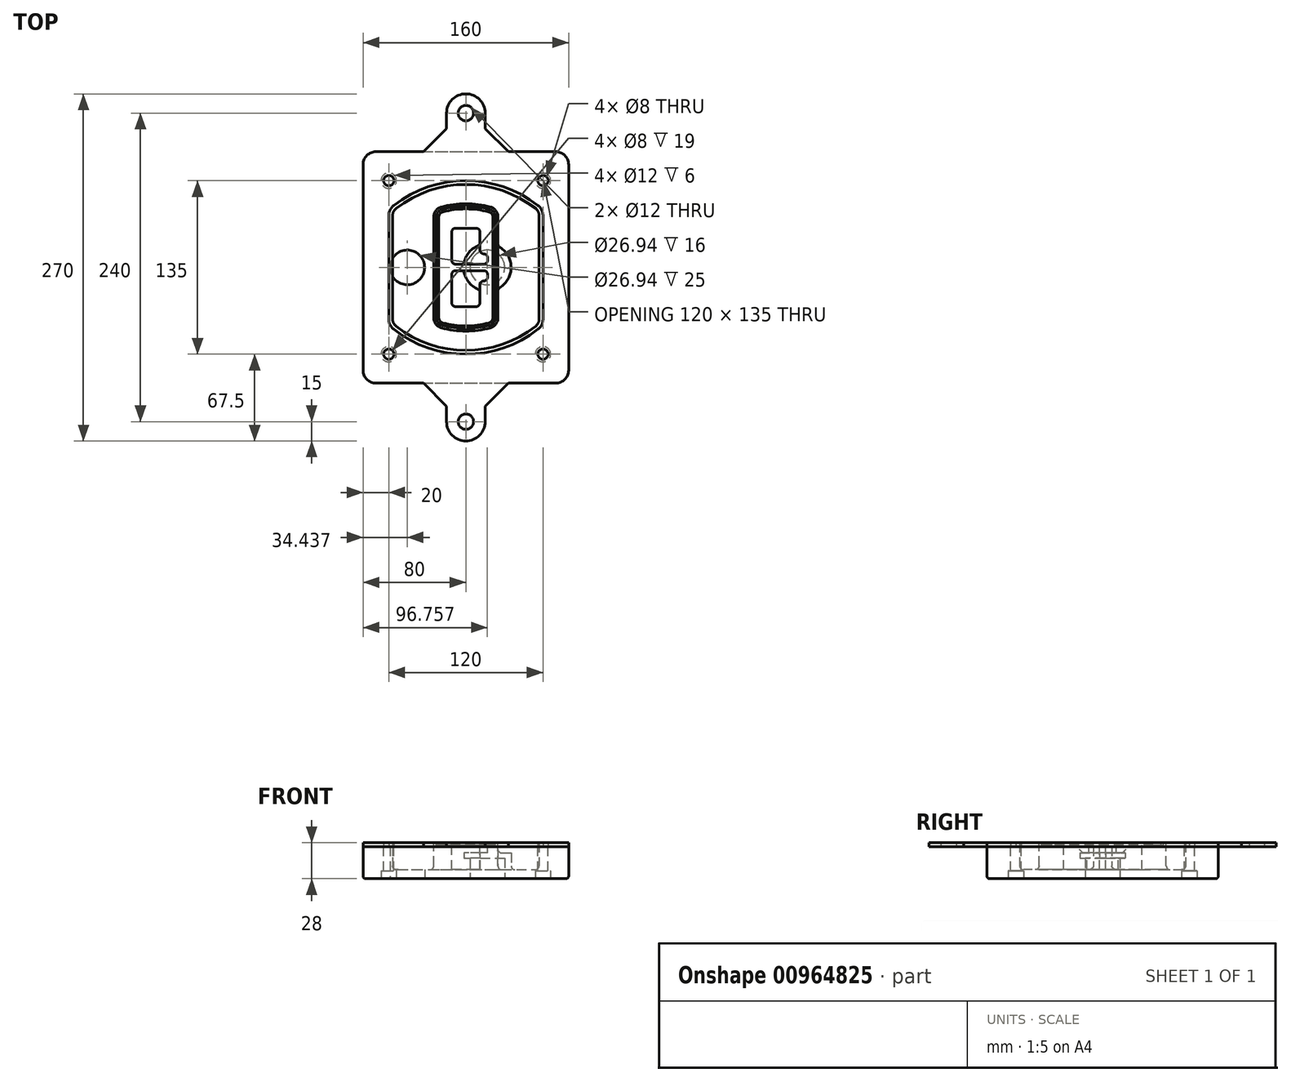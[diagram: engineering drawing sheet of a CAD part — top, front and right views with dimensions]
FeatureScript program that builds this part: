
annotation { "Feature Type Name" : "Feature", "Feature Type Description" : "" }
export const myFeature = defineFeature(function(context is Context, id is Id, definition is map)
    precondition{}
    {
        {
            var Q0;
            Q0=qCreatedBy(makeId("Top.planeOp"),FACE);
            var sketch = newSketch(context, id + "F0", { "sketchPlane" : qUnion([Q0])});
            skPoint(sketch, "E0.rect.middle", {"position": v(0, 0) * mm});
            skLineSegment(sketch, "E1.bottom", {"start": v(-70, -90) * mm, "end": v(70, -90) * mm});
            skLineSegment(sketch, "E1.top", {"start": v(-70, 90) * mm, "end": v(70, 90) * mm});
            skLineSegment(sketch, "E1.left", {"start": v(-80, -80) * mm, "end": v(-80, 80) * mm});
            skLineSegment(sketch, "E1.right", {"start": v(80, -80) * mm, "end": v(80, 80) * mm});
            skLineSegment(sketch, "E2", {"start": v(-80, 90) * mm, "end": v(80, -90) * mm, "construction": true});
            skLineSegment(sketch, "E3", {"start": v(80, 90) * mm, "end": v(-80, -90) * mm, "construction": true});
            skCircle(sketch, "E4", {"center": v(-60, 67.5) * mm, "radius": 4 * mm});
            skCircle(sketch, "E5", {"center": v(60, 67.5) * mm, "radius": 4 * mm});
            skCircle(sketch, "E6", {"center": v(60, -67.5) * mm, "radius": 4 * mm});
            skCircle(sketch, "E7", {"center": v(-60, -67.5) * mm, "radius": 4 * mm});
            skLineSegment(sketch, "E8", {"start": v(-60, 67.5) * mm, "end": v(60, 67.5) * mm, "construction": true});
            skLineSegment(sketch, "E9", {"start": v(60, 67.5) * mm, "end": v(60, -67.5) * mm, "construction": true});
            skLineSegment(sketch, "E10", {"start": v(60, -67.5) * mm, "end": v(-60, -67.5) * mm, "construction": true});
            skLineSegment(sketch, "E11", {"start": v(-60, -67.5) * mm, "end": v(-60, 67.5) * mm, "construction": true});
            skLineSegment(sketch, "E12", {"start": v(-60, 40.3) * mm, "end": v(-60, -40.3) * mm});
            skLineSegment(sketch, "E13", {"start": v(60, 40.3) * mm, "end": v(60, -40.3) * mm});
            skArc(sketch, "E14", {"start": v(56.15, 48.18) * mm, "mid": v(0, 67.5) * mm, "end": v(-56.15, 48.18) * mm});
            skArc(sketch, "E15", {"start": v(-56.15, -48.18) * mm, "mid": v(0, -67.5) * mm, "end": v(56.15, -48.18) * mm});
            skLineSegment(sketch, "E16", {"start": v(-60, 0) * mm, "end": v(60, 0) * mm, "construction": true});
            skPoint(sketch, "E17.visualSharp", {"position": v(-60, -45) * mm});
            skArc(sketch, "E17.filletArc", {"start": v(-60, -40.3) * mm, "mid": v(-58.99, -44.68) * mm, "end": v(-56.15, -48.18) * mm});
            skPoint(sketch, "E18.visualSharp", {"position": v(-60, 45) * mm});
            skArc(sketch, "E18.filletArc", {"start": v(-56.15, 48.18) * mm, "mid": v(-58.99, 44.68) * mm, "end": v(-60, 40.3) * mm});
            skPoint(sketch, "E19.visualSharp", {"position": v(60, 45) * mm});
            skArc(sketch, "E19.filletArc", {"start": v(60, 40.3) * mm, "mid": v(58.99, 44.68) * mm, "end": v(56.15, 48.18) * mm});
            skPoint(sketch, "E20.visualSharp", {"position": v(60, -45) * mm});
            skArc(sketch, "E20.filletArc", {"start": v(56.15, -48.18) * mm, "mid": v(58.99, -44.68) * mm, "end": v(60, -40.3) * mm});
            skPoint(sketch, "E21.visualSharp", {"position": v(-80, 90) * mm});
            skArc(sketch, "E21.filletArc", {"start": v(-70, 90) * mm, "mid": v(-77.07, 87.07) * mm, "end": v(-80, 80) * mm});
            skPoint(sketch, "E22.visualSharp", {"position": v(80, 90) * mm});
            skArc(sketch, "E22.filletArc", {"start": v(80, 80) * mm, "mid": v(77.07, 87.07) * mm, "end": v(70, 90) * mm});
            skPoint(sketch, "E23.visualSharp", {"position": v(80, -90) * mm});
            skArc(sketch, "E23.filletArc", {"start": v(70, -90) * mm, "mid": v(77.07, -87.07) * mm, "end": v(80, -80) * mm});
            skPoint(sketch, "E24.visualSharp", {"position": v(-80, -90) * mm});
            skArc(sketch, "E24.filletArc", {"start": v(-80, -80) * mm, "mid": v(-77.07, -87.07) * mm, "end": v(-70, -90) * mm});
            skArc(sketch, "E25.0", {"start": v(57, 40.3) * mm, "mid": v(56.3, 43.36) * mm, "end": v(54.3, 45.81) * mm});
            skLineSegment(sketch, "E25.1", {"start": v(57, 40.3) * mm, "end": v(57, -40.3) * mm});
            skArc(sketch, "E25.2", {"start": v(54.3, -45.81) * mm, "mid": v(56.3, -43.36) * mm, "end": v(57, -40.3) * mm});
            skArc(sketch, "E25.3", {"start": v(-54.3, -45.81) * mm, "mid": v(0, -64.5) * mm, "end": v(54.3, -45.81) * mm});
            skArc(sketch, "E25.4", {"start": v(-57, -40.3) * mm, "mid": v(-56.3, -43.36) * mm, "end": v(-54.3, -45.81) * mm});
            skArc(sketch, "E25.5", {"start": v(54.3, 45.81) * mm, "mid": v(0, 64.5) * mm, "end": v(-54.3, 45.81) * mm});
            skLineSegment(sketch, "E25.6", {"start": v(-57, 40.3) * mm, "end": v(-57, -40.3) * mm});
            skArc(sketch, "E25.7", {"start": v(-54.3, 45.81) * mm, "mid": v(-56.3, 43.36) * mm, "end": v(-57, 40.3) * mm});
            skArc(sketch, "E26.0", {"start": v(-58.62, 51.33) * mm, "mid": v(-62.58, 46.43) * mm, "end": v(-64, 40.3) * mm});
            skArc(sketch, "E26.1", {"start": v(58.62, 51.33) * mm, "mid": v(0, 71.5) * mm, "end": v(-58.62, 51.33) * mm});
            skArc(sketch, "E26.2", {"start": v(64, 40.3) * mm, "mid": v(62.58, 46.43) * mm, "end": v(58.62, 51.33) * mm});
            skLineSegment(sketch, "E26.3", {"start": v(64, 40.3) * mm, "end": v(64, -40.3) * mm});
            skArc(sketch, "E26.4", {"start": v(58.62, -51.33) * mm, "mid": v(62.58, -46.43) * mm, "end": v(64, -40.3) * mm});
            skLineSegment(sketch, "E26.5", {"start": v(-64, 40.3) * mm, "end": v(-64, -40.3) * mm});
            skArc(sketch, "E26.6", {"start": v(-58.62, -51.33) * mm, "mid": v(0, -71.5) * mm, "end": v(58.62, -51.33) * mm});
            skArc(sketch, "E26.7", {"start": v(-64, -40.3) * mm, "mid": v(-62.58, -46.43) * mm, "end": v(-58.62, -51.33) * mm});
            skSolve(sketch);
        }
        {
            var Q0;
            Q0=makeQuery(id+"F0.imprint","IMPRINT",FACE,{"disambiguationData":[TD([[makeQuery(id+"F0.imprint","IMPRINT",EDGE,{"derivedFrom":sQuery(id+"F0.wireOp",EDGE,"E1.bottom")}),1.0]])]});
            var Q1;
            Q1=makeQuery(id+"F0.imprint","IMPRINT",FACE,{"disambiguationData":[TD([[makeQuery(id+"F0.imprint","IMPRINT",EDGE,{"derivedFrom":sQuery(id+"F0.wireOp",EDGE,"E12")}),1.0]])]});
            var Q2;
            Q2=makeQuery(id+"F0.imprint","IMPRINT",FACE,{"disambiguationData":[TD([[makeQuery(id+"F0.imprint","IMPRINT",EDGE,{"derivedFrom":sQuery(id+"F0.wireOp",EDGE,"E25.0")}),1.0]])]});
            var Q3;
            Q3=makeQuery(id+"F0.imprint","IMPRINT",FACE,{"disambiguationData":[TD([[makeQuery(id+"F0.imprint","IMPRINT",EDGE,{"derivedFrom":sQuery(id+"F0.wireOp",EDGE,"E12")}),-1.0]])]});
            extrude(context, id + "F1", {"entities" : qUnion([Q0, Q1, Q2, Q3]), "oppositeDirection" : true, "depth" : 25 * mm});
        }
        {
            var Q0;
            Q0=makeQuery(id+"F0.imprint","IMPRINT",FACE,{"disambiguationData":[TD([[makeQuery(id+"F0.imprint","IMPRINT",EDGE,{"derivedFrom":sQuery(id+"F0.wireOp",EDGE,"E12")}),1.0]])]});
            extrude(context, id + "F2", {"entities" : qUnion([Q0]), "operationType" : NewBodyOperationType.ADD, "depth" : 3 * mm});
        }
        {
            var Q0;
            Q0=makeQuery(id+"F0.imprint","IMPRINT",FACE,{"disambiguationData":[TD([[makeQuery(id+"F0.imprint","IMPRINT",EDGE,{"derivedFrom":sQuery(id+"F0.wireOp",EDGE,"E25.0")}),1.0]])]});
            extrude(context, id + "F3", {"entities" : qUnion([Q0]), "operationType" : NewBodyOperationType.REMOVE, "oppositeDirection" : true, "depth" : 18 * mm});
        }
        {
            var Q0;
            Q0=makeQuery(id+"F2.opExtrude","CAP_FACE",FACE,{"disambiguationData":[OSD([sQuery(id+"F0.wireOp",EDGE,"E12"),sQuery(id+"F0.wireOp",EDGE,"E13"),sQuery(id+"F0.wireOp",EDGE,"E14"),sQuery(id+"F0.wireOp",EDGE,"E15"),sQuery(id+"F0.wireOp",EDGE,"E17.filletArc"),sQuery(id+"F0.wireOp",EDGE,"E18.filletArc"),sQuery(id+"F0.wireOp",EDGE,"E19.filletArc"),sQuery(id+"F0.wireOp",EDGE,"E20.filletArc"),sQuery(id+"F0.wireOp",EDGE,"E25.0"),sQuery(id+"F0.wireOp",EDGE,"E25.1"),sQuery(id+"F0.wireOp",EDGE,"E25.2"),sQuery(id+"F0.wireOp",EDGE,"E25.3"),sQuery(id+"F0.wireOp",EDGE,"E25.4"),sQuery(id+"F0.wireOp",EDGE,"E25.5"),sQuery(id+"F0.wireOp",EDGE,"E25.6"),sQuery(id+"F0.wireOp",EDGE,"E25.7")])],"isStart":false});
            var sketch = newSketch(context, id + "F4", { "sketchPlane" : qUnion([Q0])});
            skArc(sketch, "E27.0", {"start": v(-19.08, -46.97) * mm, "mid": v(0, -49.5) * mm, "end": v(19.08, -46.97) * mm});
            skArc(sketch, "E28.0", {"start": v(19.08, 46.97) * mm, "mid": v(0, 49.5) * mm, "end": v(-19.08, 46.97) * mm});
            skLineSegment(sketch, "E29", {"start": v(-25, 39.25) * mm, "end": v(-25, -39.25) * mm});
            skLineSegment(sketch, "E30", {"start": v(25, 39.25) * mm, "end": v(25, -39.25) * mm});
            skLineSegment(sketch, "E31", {"start": v(-25, 45.1) * mm, "end": v(25, 45.1) * mm, "construction": true});
            skLineSegment(sketch, "E32", {"start": v(-25, -45.1) * mm, "end": v(25, -45.1) * mm, "construction": true});
            skPoint(sketch, "E33.visualSharp", {"position": v(-25, 45.1) * mm});
            skArc(sketch, "E33.filletArc", {"start": v(-19.08, 46.97) * mm, "mid": v(-23.35, 44.11) * mm, "end": v(-25, 39.25) * mm});
            skPoint(sketch, "E34.visualSharp", {"position": v(25, 45.1) * mm});
            skArc(sketch, "E34.filletArc", {"start": v(25, 39.25) * mm, "mid": v(23.35, 44.11) * mm, "end": v(19.08, 46.97) * mm});
            skPoint(sketch, "E35.visualSharp", {"position": v(25, -45.1) * mm});
            skArc(sketch, "E35.filletArc", {"start": v(19.08, -46.97) * mm, "mid": v(23.35, -44.11) * mm, "end": v(25, -39.25) * mm});
            skPoint(sketch, "E36.visualSharp", {"position": v(-25, -45.1) * mm});
            skArc(sketch, "E36.filletArc", {"start": v(-25, -39.25) * mm, "mid": v(-23.35, -44.11) * mm, "end": v(-19.08, -46.97) * mm});
            skArc(sketch, "E37.0", {"start": v(54.3, 45.81) * mm, "mid": v(0, 64.5) * mm, "end": v(-54.3, 45.81) * mm});
            skArc(sketch, "E37.1", {"start": v(-54.3, 45.81) * mm, "mid": v(-56.3, 43.36) * mm, "end": v(-57, 40.3) * mm});
            skLineSegment(sketch, "E37.2", {"start": v(-57, 40.3) * mm, "end": v(-57, -40.3) * mm});
            skArc(sketch, "E37.3", {"start": v(-57, -40.3) * mm, "mid": v(-56.3, -43.36) * mm, "end": v(-54.3, -45.81) * mm});
            skArc(sketch, "E37.4", {"start": v(-54.3, -45.81) * mm, "mid": v(0, -64.5) * mm, "end": v(54.3, -45.81) * mm});
            skArc(sketch, "E37.5", {"start": v(54.3, -45.81) * mm, "mid": v(56.3, -43.36) * mm, "end": v(57, -40.3) * mm});
            skLineSegment(sketch, "E37.6", {"start": v(57, 40.3) * mm, "end": v(57, -40.3) * mm});
            skArc(sketch, "E37.7", {"start": v(57, 40.3) * mm, "mid": v(56.3, 43.36) * mm, "end": v(54.3, 45.81) * mm});
            skLineSegment(sketch, "E38.0", {"start": v(23, 39.25) * mm, "end": v(23, -39.25) * mm});
            skArc(sketch, "E38.1", {"start": v(18.56, -45.04) * mm, "mid": v(21.76, -42.9) * mm, "end": v(23, -39.25) * mm});
            skArc(sketch, "E38.2", {"start": v(-18.56, -45.04) * mm, "mid": v(0, -47.5) * mm, "end": v(18.56, -45.04) * mm});
            skArc(sketch, "E38.3", {"start": v(-23, -39.25) * mm, "mid": v(-21.76, -42.9) * mm, "end": v(-18.56, -45.04) * mm});
            skLineSegment(sketch, "E38.4", {"start": v(-23, 39.25) * mm, "end": v(-23, -39.25) * mm});
            skArc(sketch, "E38.5", {"start": v(23, 39.25) * mm, "mid": v(21.76, 42.9) * mm, "end": v(18.56, 45.04) * mm});
            skArc(sketch, "E38.6", {"start": v(-18.56, 45.04) * mm, "mid": v(-21.76, 42.9) * mm, "end": v(-23, 39.25) * mm});
            skArc(sketch, "E38.7", {"start": v(18.56, 45.04) * mm, "mid": v(0, 47.5) * mm, "end": v(-18.56, 45.04) * mm});
            skArc(sketch, "E39.0", {"start": v(21, 39.25) * mm, "mid": v(20.18, 41.68) * mm, "end": v(18.04, 43.1) * mm});
            skLineSegment(sketch, "E39.1", {"start": v(21, 39.25) * mm, "end": v(21, -39.25) * mm});
            skArc(sketch, "E39.2", {"start": v(18.04, -43.1) * mm, "mid": v(20.18, -41.68) * mm, "end": v(21, -39.25) * mm});
            skArc(sketch, "E39.3", {"start": v(-18.04, -43.1) * mm, "mid": v(0, -45.5) * mm, "end": v(18.04, -43.1) * mm});
            skArc(sketch, "E39.4", {"start": v(-21, -39.25) * mm, "mid": v(-20.18, -41.68) * mm, "end": v(-18.04, -43.1) * mm});
            skArc(sketch, "E39.5", {"start": v(18.04, 43.1) * mm, "mid": v(0, 45.5) * mm, "end": v(-18.04, 43.1) * mm});
            skLineSegment(sketch, "E39.6", {"start": v(-21, 39.25) * mm, "end": v(-21, -39.25) * mm});
            skArc(sketch, "E39.7", {"start": v(-18.04, 43.1) * mm, "mid": v(-20.18, 41.68) * mm, "end": v(-21, 39.25) * mm});
            skLineSegment(sketch, "E40", {"start": v(-25, 0) * mm, "end": v(25, 0) * mm, "construction": true});
            skLineSegment(sketch, "E41", {"start": v(-11, 5.5) * mm, "end": v(-11, 27.5) * mm});
            skLineSegment(sketch, "E42", {"start": v(-8, 30.5) * mm, "end": v(8, 30.5) * mm});
            skLineSegment(sketch, "E43", {"start": v(11, 27.5) * mm, "end": v(11, 13.5) * mm});
            skLineSegment(sketch, "E44", {"start": v(14, 10.5) * mm, "end": v(14, 10.5) * mm});
            skLineSegment(sketch, "E45", {"start": v(17, 7.5) * mm, "end": v(17, 5.5) * mm});
            skLineSegment(sketch, "E46", {"start": v(14, 2.5) * mm, "end": v(-8, 2.5) * mm});
            skPoint(sketch, "E47.visualSharp", {"position": v(-11, 30.5) * mm});
            skArc(sketch, "E47.filletArc", {"start": v(-8, 30.5) * mm, "mid": v(-10.12, 29.62) * mm, "end": v(-11, 27.5) * mm});
            skPoint(sketch, "E48.visualSharp", {"position": v(11, 30.5) * mm});
            skArc(sketch, "E48.filletArc", {"start": v(11, 27.5) * mm, "mid": v(10.12, 29.62) * mm, "end": v(8, 30.5) * mm});
            skPoint(sketch, "E49.visualSharp", {"position": v(11, 10.5) * mm});
            skArc(sketch, "E49.filletArc", {"start": v(11, 13.5) * mm, "mid": v(11.88, 11.38) * mm, "end": v(14, 10.5) * mm});
            skPoint(sketch, "E50.visualSharp", {"position": v(17, 10.5) * mm});
            skArc(sketch, "E50.filletArc", {"start": v(17, 7.5) * mm, "mid": v(16.12, 9.62) * mm, "end": v(14, 10.5) * mm});
            skPoint(sketch, "E51.visualSharp", {"position": v(17, 2.5) * mm});
            skArc(sketch, "E51.filletArc", {"start": v(14, 2.5) * mm, "mid": v(16.12, 3.38) * mm, "end": v(17, 5.5) * mm});
            skPoint(sketch, "E52.visualSharp", {"position": v(-11, 2.5) * mm});
            skArc(sketch, "E52.filletArc", {"start": v(-11, 5.5) * mm, "mid": v(-10.12, 3.38) * mm, "end": v(-8, 2.5) * mm});
            skLineSegment(sketch, "E53.0.MirrorCS", {"start": v(14, -2.5) * mm, "end": v(-8, -2.5) * mm});
            skArc(sketch, "E54.0.MirrorCS", {"start": v(-11, -5.5) * mm, "mid": v(-10.12, -3.38) * mm, "end": v(-8, -2.5) * mm});
            skLineSegment(sketch, "E55.0.MirrorCS", {"start": v(-11, -5.5) * mm, "end": v(-11, -27.5) * mm});
            skArc(sketch, "E56.0.MirrorCS", {"start": v(-8, -30.5) * mm, "mid": v(-10.12, -29.62) * mm, "end": v(-11, -27.5) * mm});
            skLineSegment(sketch, "E57.0.MirrorCS", {"start": v(-8, -30.5) * mm, "end": v(8, -30.5) * mm});
            skArc(sketch, "E58.0.MirrorCS", {"start": v(11, -27.5) * mm, "mid": v(10.12, -29.62) * mm, "end": v(8, -30.5) * mm});
            skLineSegment(sketch, "E59.0.MirrorCS", {"start": v(11, -27.5) * mm, "end": v(11, -13.5) * mm});
            skArc(sketch, "E60.0.MirrorCS", {"start": v(11, -13.5) * mm, "mid": v(11.88, -11.38) * mm, "end": v(14, -10.5) * mm});
            skArc(sketch, "E61.0.MirrorCS", {"start": v(17, -7.5) * mm, "mid": v(16.12, -9.62) * mm, "end": v(14, -10.5) * mm});
            skLineSegment(sketch, "E62.0.MirrorCS", {"start": v(17, -7.5) * mm, "end": v(17, -5.5) * mm});
            skArc(sketch, "E63.0.MirrorCS", {"start": v(14, -2.5) * mm, "mid": v(16.12, -3.38) * mm, "end": v(17, -5.5) * mm});
            skSolve(sketch);
        }
        {
            var Q0;
            Q0=makeQuery(id+"F4.imprint","IMPRINT",FACE,{"disambiguationData":[TD([[makeQuery(id+"F4.imprint","IMPRINT",EDGE,{"derivedFrom":sQuery(id+"F4.wireOp",EDGE,"E27.0")}),1.0]])]});
            var Q1;
            Q1=makeQuery(id+"F4.imprint","IMPRINT",FACE,{"disambiguationData":[TD([[makeQuery(id+"F4.imprint","IMPRINT",EDGE,{"derivedFrom":sQuery(id+"F4.wireOp",EDGE,"E38.0")}),-1.0]])]});
            var Q2;
            Q2=makeQuery(id+"F4.imprint","IMPRINT",FACE,{"disambiguationData":[TD([[makeQuery(id+"F4.imprint","IMPRINT",EDGE,{"derivedFrom":sQuery(id+"F4.wireOp",EDGE,"E39.0")}),1.0]])]});
            extrude(context, id + "F5", {"entities" : qUnion([Q0, Q1, Q2]), "operationType" : NewBodyOperationType.ADD, "endBound" : BoundingType.UP_TO_NEXT, "oppositeDirection" : true, "depth" : 25 * mm});
        }
        {
            var Q0;
            Q0=makeQuery(id+"F4.imprint","IMPRINT",FACE,{"disambiguationData":[TD([[makeQuery(id+"F4.imprint","IMPRINT",EDGE,{"derivedFrom":sQuery(id+"F4.wireOp",EDGE,"E38.0")}),-1.0]])]});
            extrude(context, id + "F6", {"entities" : qUnion([Q0]), "operationType" : NewBodyOperationType.REMOVE, "oppositeDirection" : true, "depth" : 2 * mm});
        }
        {
            var Q0;
            Q0=makeQuery(id+"F1.opExtrude","CAP_FACE",FACE,{"disambiguationData":[OSD([sQuery(id+"F0.wireOp",EDGE,"E1.bottom"),sQuery(id+"F0.wireOp",EDGE,"E1.top"),sQuery(id+"F0.wireOp",EDGE,"E1.left"),sQuery(id+"F0.wireOp",EDGE,"E1.right"),sQuery(id+"F0.wireOp",EDGE,"E4"),sQuery(id+"F0.wireOp",EDGE,"E5"),sQuery(id+"F0.wireOp",EDGE,"E6"),sQuery(id+"F0.wireOp",EDGE,"E7"),sQuery(id+"F0.wireOp",EDGE,"E21.filletArc"),sQuery(id+"F0.wireOp",EDGE,"E22.filletArc"),sQuery(id+"F0.wireOp",EDGE,"E23.filletArc"),sQuery(id+"F0.wireOp",EDGE,"E24.filletArc")])],"isStart":false});
            var sketch = newSketch(context, id + "F7", { "sketchPlane" : qUnion([Q0])});
            skCircle(sketch, "E64", {"center": v(16.76, 0) * mm, "radius": 13.47 * mm});
            skCircle(sketch, "E65", {"center": v(-45.56, 0) * mm, "radius": 13.47 * mm});
            skLineSegment(sketch, "E66", {"start": v(80, 0) * mm, "end": v(-80, 0) * mm});
            skCircle(sketch, "E67", {"center": v(16.76, 0) * mm, "radius": 18.47 * mm});
            skCircle(sketch, "E68", {"center": v(60, -67.5) * mm, "radius": 6 * mm});
            skCircle(sketch, "E69", {"center": v(-60, -67.5) * mm, "radius": 6 * mm});
            skCircle(sketch, "E70", {"center": v(-60, 67.5) * mm, "radius": 6 * mm});
            skCircle(sketch, "E71", {"center": v(60, 67.5) * mm, "radius": 6 * mm});
            skSolve(sketch);
        }
        {
            var Q0;
            {var subQ1=sQuery(id+"F7.wireOp",EDGE,"E66");var subQ4=sQuery(id+"F7.wireOp",EDGE,"E64");var subQ6=makeQuery(id+"F7.imprint","INTERSECT",VERTEX,{"disambiguationData":[OD(0.0)],"derivedFrom":[subQ4,subQ1]});Q0=makeQuery(id+"F7.imprint","IMPRINT",FACE,{"disambiguationData":[TD([[makeQuery(id+"F7.imprint","IMPRINT",EDGE,{"disambiguationData":[TD([[subQ6,-1.0]])],"derivedFrom":subQ4}),-1.0]])]});}
            var Q1;
            {var subQ0=sQuery(id+"F7.wireOp",EDGE,"E66");var subQ1=sQuery(id+"F7.wireOp",EDGE,"E64");var subQ3=makeQuery(id+"F7.imprint","INTERSECT",VERTEX,{"disambiguationData":[OD(0.0)],"derivedFrom":[subQ1,subQ0]});Q1=makeQuery(id+"F7.imprint","IMPRINT",FACE,{"disambiguationData":[TD([[makeQuery(id+"F7.imprint","IMPRINT",EDGE,{"disambiguationData":[TD([[subQ3,-1.0]])],"derivedFrom":subQ1}),1.0]])]});}
            var Q2;
            {var subQ0=sQuery(id+"F7.wireOp",EDGE,"E66");var subQ1=sQuery(id+"F7.wireOp",EDGE,"E64");var subQ3=makeQuery(id+"F7.imprint","INTERSECT",VERTEX,{"disambiguationData":[OD(0.0)],"derivedFrom":[subQ1,subQ0]});Q2=makeQuery(id+"F7.imprint","IMPRINT",FACE,{"disambiguationData":[TD([[makeQuery(id+"F7.imprint","IMPRINT",EDGE,{"disambiguationData":[TD([[subQ3,1.0]])],"derivedFrom":subQ1}),1.0]])]});}
            var Q3;
            {var subQ1=sQuery(id+"F7.wireOp",EDGE,"E66");var subQ4=sQuery(id+"F7.wireOp",EDGE,"E64");var subQ6=makeQuery(id+"F7.imprint","INTERSECT",VERTEX,{"disambiguationData":[OD(0.0)],"derivedFrom":[subQ4,subQ1]});Q3=makeQuery(id+"F7.imprint","IMPRINT",FACE,{"disambiguationData":[TD([[makeQuery(id+"F7.imprint","IMPRINT",EDGE,{"disambiguationData":[TD([[subQ6,1.0]])],"derivedFrom":subQ4}),-1.0]])]});}
            extrude(context, id + "F8", {"entities" : qUnion([Q0, Q1, Q2, Q3]), "operationType" : NewBodyOperationType.ADD, "oppositeDirection" : true, "depth" : 20 * mm});
        }
        {
            var Q0;
            {var subQ0=sQuery(id+"F7.wireOp",EDGE,"E66");var subQ1=sQuery(id+"F7.wireOp",EDGE,"E64");var subQ3=makeQuery(id+"F7.imprint","INTERSECT",VERTEX,{"disambiguationData":[OD(0.0)],"derivedFrom":[subQ1,subQ0]});Q0=makeQuery(id+"F7.imprint","IMPRINT",FACE,{"disambiguationData":[TD([[makeQuery(id+"F7.imprint","IMPRINT",EDGE,{"disambiguationData":[TD([[subQ3,-1.0]])],"derivedFrom":subQ1}),1.0]])]});}
            var Q1;
            {var subQ0=sQuery(id+"F7.wireOp",EDGE,"E66");var subQ1=sQuery(id+"F7.wireOp",EDGE,"E64");var subQ3=makeQuery(id+"F7.imprint","INTERSECT",VERTEX,{"disambiguationData":[OD(0.0)],"derivedFrom":[subQ1,subQ0]});Q1=makeQuery(id+"F7.imprint","IMPRINT",FACE,{"disambiguationData":[TD([[makeQuery(id+"F7.imprint","IMPRINT",EDGE,{"disambiguationData":[TD([[subQ3,1.0]])],"derivedFrom":subQ1}),1.0]])]});}
            extrude(context, id + "F9", {"entities" : qUnion([Q0, Q1]), "operationType" : NewBodyOperationType.REMOVE, "oppositeDirection" : true, "depth" : 16 * mm});
        }
        {
            var Q0;
            {var subQ0=sQuery(id+"F7.wireOp",EDGE,"E66");var subQ1=sQuery(id+"F7.wireOp",EDGE,"E65");var subQ3=makeQuery(id+"F7.imprint","INTERSECT",VERTEX,{"disambiguationData":[OD(0.0)],"derivedFrom":[subQ1,subQ0]});Q0=makeQuery(id+"F7.imprint","IMPRINT",FACE,{"disambiguationData":[TD([[makeQuery(id+"F7.imprint","IMPRINT",EDGE,{"disambiguationData":[TD([[subQ3,-1.0]])],"derivedFrom":subQ1}),1.0]])]});}
            var Q1;
            {var subQ0=sQuery(id+"F7.wireOp",EDGE,"E66");var subQ1=sQuery(id+"F7.wireOp",EDGE,"E65");var subQ3=makeQuery(id+"F7.imprint","INTERSECT",VERTEX,{"disambiguationData":[OD(0.0)],"derivedFrom":[subQ1,subQ0]});Q1=makeQuery(id+"F7.imprint","IMPRINT",FACE,{"disambiguationData":[TD([[makeQuery(id+"F7.imprint","IMPRINT",EDGE,{"disambiguationData":[TD([[subQ3,1.0]])],"derivedFrom":subQ1}),1.0]])]});}
            extrude(context, id + "F10", {"entities" : qUnion([Q0, Q1]), "operationType" : NewBodyOperationType.REMOVE, "oppositeDirection" : true, "depth" : 25 * mm});
        }
        {
            var Q0;
            Q0=makeQuery(id+"F7.imprint","IMPRINT",FACE,{"disambiguationData":[TD([[makeQuery(id+"F7.imprint","IMPRINT",EDGE,{"derivedFrom":sQuery(id+"F7.wireOp",EDGE,"E68")}),1.0]])]});
            var Q1;
            Q1=makeQuery(id+"F7.imprint","IMPRINT",FACE,{"disambiguationData":[TD([[makeQuery(id+"F7.imprint","IMPRINT",EDGE,{"derivedFrom":makeQuery(id+"F1.opExtrude","CAP_EDGE",EDGE,{"disambiguationData":[OSD([sQuery(id+"F0.wireOp",EDGE,"E5")])],"isStart":false})}),-1.0]])]});
            var Q2;
            Q2=makeQuery(id+"F7.imprint","IMPRINT",FACE,{"disambiguationData":[TD([[makeQuery(id+"F7.imprint","IMPRINT",EDGE,{"derivedFrom":sQuery(id+"F7.wireOp",EDGE,"E69")}),1.0]])]});
            var Q3;
            Q3=makeQuery(id+"F7.imprint","IMPRINT",FACE,{"disambiguationData":[TD([[makeQuery(id+"F7.imprint","IMPRINT",EDGE,{"derivedFrom":makeQuery(id+"F1.opExtrude","CAP_EDGE",EDGE,{"disambiguationData":[OSD([sQuery(id+"F0.wireOp",EDGE,"E4")])],"isStart":false})}),-1.0]])]});
            var Q4;
            Q4=makeQuery(id+"F7.imprint","IMPRINT",FACE,{"disambiguationData":[TD([[makeQuery(id+"F7.imprint","IMPRINT",EDGE,{"derivedFrom":sQuery(id+"F7.wireOp",EDGE,"E70")}),1.0]])]});
            var Q5;
            Q5=makeQuery(id+"F7.imprint","IMPRINT",FACE,{"disambiguationData":[TD([[makeQuery(id+"F7.imprint","IMPRINT",EDGE,{"derivedFrom":makeQuery(id+"F1.opExtrude","CAP_EDGE",EDGE,{"disambiguationData":[OSD([sQuery(id+"F0.wireOp",EDGE,"E7")])],"isStart":false})}),-1.0]])]});
            var Q6;
            Q6=makeQuery(id+"F7.imprint","IMPRINT",FACE,{"disambiguationData":[TD([[makeQuery(id+"F7.imprint","IMPRINT",EDGE,{"derivedFrom":sQuery(id+"F7.wireOp",EDGE,"E71")}),1.0]])]});
            var Q7;
            Q7=makeQuery(id+"F7.imprint","IMPRINT",FACE,{"disambiguationData":[TD([[makeQuery(id+"F7.imprint","IMPRINT",EDGE,{"derivedFrom":makeQuery(id+"F1.opExtrude","CAP_EDGE",EDGE,{"disambiguationData":[OSD([sQuery(id+"F0.wireOp",EDGE,"E6")])],"isStart":false})}),-1.0]])]});
            extrude(context, id + "F11", {"entities" : qUnion([Q0, Q1, Q2, Q3, Q4, Q5, Q6, Q7]), "operationType" : NewBodyOperationType.REMOVE, "oppositeDirection" : true, "depth" : 6 * mm});
        }
        {
            var Q0;
            Q0=makeQuery(id+"F9.boolean.opBoolean","COPY",FACE,{"derivedFrom":makeQuery(id+"F9.opExtrude","CAP_FACE",FACE,{"disambiguationData":[OSD([sQuery(id+"F7.wireOp",EDGE,"E64")])],"isStart":false})});
            var sketch = newSketch(context, id + "F12", { "sketchPlane" : qUnion([Q0])});
            skArc(sketch, "E72.0", {"start": v(11, 17.55) * mm, "mid": v(2.57, 11.82) * mm, "end": v(-1.54, 2.5) * mm});
            skArc(sketch, "E72.1", {"start": v(-1.54, -2.5) * mm, "mid": v(2.57, -11.82) * mm, "end": v(11, -17.55) * mm});
            skLineSegment(sketch, "E73", {"start": v(-1.54, -2.5) * mm, "end": v(14, -2.5) * mm});
            skLineSegment(sketch, "E74.0", {"start": v(14, 2.5) * mm, "end": v(-1.54, 2.5) * mm});
            skArc(sketch, "E74.1", {"start": v(14, 2.5) * mm, "mid": v(16.12, 3.38) * mm, "end": v(17, 5.5) * mm});
            skLineSegment(sketch, "E74.2", {"start": v(17, 7.5) * mm, "end": v(17, 5.5) * mm});
            skArc(sketch, "E74.3", {"start": v(17, 7.5) * mm, "mid": v(16.12, 9.62) * mm, "end": v(14, 10.5) * mm});
            skArc(sketch, "E74.4", {"start": v(11, 13.5) * mm, "mid": v(11.88, 11.38) * mm, "end": v(14, 10.5) * mm});
            skLineSegment(sketch, "E74.5", {"start": v(11, 17.55) * mm, "end": v(11, 13.5) * mm});
            skLineSegment(sketch, "E74.7", {"start": v(14, -2.5) * mm, "end": v(-1.54, -2.5) * mm});
            skArc(sketch, "E74.8", {"start": v(14, -2.5) * mm, "mid": v(16.12, -3.38) * mm, "end": v(17, -5.5) * mm});
            skLineSegment(sketch, "E74.9", {"start": v(17, -7.5) * mm, "end": v(17, -5.5) * mm});
            skArc(sketch, "E74.10", {"start": v(17, -7.5) * mm, "mid": v(16.12, -9.62) * mm, "end": v(14, -10.5) * mm});
            skArc(sketch, "E74.11", {"start": v(11, -13.5) * mm, "mid": v(11.88, -11.38) * mm, "end": v(14, -10.5) * mm});
            skLineSegment(sketch, "E74.12", {"start": v(11, -17.55) * mm, "end": v(11, -13.5) * mm});
            skPoint(sketch, "E75.orphan", {"position": v(11, -27.5) * mm});
            skPoint(sketch, "E76.orphan", {"position": v(-8, -2.5) * mm});
            skPoint(sketch, "E77.orphan", {"position": v(-8, 2.5) * mm});
            skPoint(sketch, "E78.orphan", {"position": v(11, 27.5) * mm});
            skSolve(sketch);
        }
        {
            var Q0;
            {var subQ7=sQuery(id+"F12.wireOp",EDGE,"E72.0");var subQ14=sQuery(id+"F12.wireOp",EDGE,"E72.1");var subQ16=sQuery(id+"F12.wireOp",EDGE,"E74.1");var subQ18=sQuery(id+"F12.wireOp",EDGE,"E74.8");Q0=qUnion([makeQuery(id+"F12.imprint","IMPRINT",FACE,{"disambiguationData":[TD([[makeQuery(id+"F12.imprint","IMPRINT",EDGE,{"derivedFrom":subQ7}),1.0]])]}),makeQuery(id+"F12.imprint","IMPRINT",FACE,{"disambiguationData":[TD([[makeQuery(id+"F12.imprint","IMPRINT",EDGE,{"derivedFrom":subQ14}),1.0]])]}),makeQuery(id+"F12.imprint","IMPRINT",FACE,{"disambiguationData":[TD([[makeQuery(id+"F12.imprint","IMPRINT",EDGE,{"derivedFrom":subQ16}),1.0]])]}),makeQuery(id+"F12.imprint","IMPRINT",FACE,{"disambiguationData":[TD([[makeQuery(id+"F12.imprint","IMPRINT",EDGE,{"derivedFrom":subQ18}),-1.0]])]})]);}
            var Q1;
            Q1=makeQuery(id+"F5.boolean.opBoolean","SPLIT",FACE,{"disambiguationData":[TD([makeQuery(id+"F5.opExtrude","SWEPT_FACE",FACE,{"disambiguationData":[OSD([sQuery(id+"F4.wireOp",EDGE,"E41")])]})])],"derivedFrom":makeQuery(id+"F3.boolean.opBoolean","COPY",FACE,{"derivedFrom":makeQuery(id+"F3.opExtrude","CAP_FACE",FACE,{"disambiguationData":[OSD([sQuery(id+"F0.wireOp",EDGE,"E25.0"),sQuery(id+"F0.wireOp",EDGE,"E25.1"),sQuery(id+"F0.wireOp",EDGE,"E25.2"),sQuery(id+"F0.wireOp",EDGE,"E25.3"),sQuery(id+"F0.wireOp",EDGE,"E25.4"),sQuery(id+"F0.wireOp",EDGE,"E25.5"),sQuery(id+"F0.wireOp",EDGE,"E25.6"),sQuery(id+"F0.wireOp",EDGE,"E25.7")])],"isStart":false})})});
            extrude(context, id + "F13", {"entities" : qUnion([Q0]), "operationType" : NewBodyOperationType.REMOVE, "endBound" : BoundingType.UP_TO_SURFACE, "endBoundEntityFace" : qUnion([Q1]), "depth" : 25 * mm});
        }
        {
            var Q0;
            Q0=makeQuery(id+"F3.boolean.opBoolean","COPY",EDGE,{"derivedFrom":makeQuery(id+"F3.opExtrude","CAP_EDGE",EDGE,{"disambiguationData":[OSD([sQuery(id+"F0.wireOp",EDGE,"E25.6")])],"isStart":false})});
            var Q1;
            Q1=makeQuery(id+"F8.boolean.opBoolean","INTERSECT",EDGE,{"derivedFrom":[makeQuery(id+"F5.opExtrude","SWEPT_FACE",FACE,{"disambiguationData":[OSD([sQuery(id+"F4.wireOp",EDGE,"E30")])]}),makeQuery(id+"F8.opExtrude","CAP_FACE",FACE,{"disambiguationData":[OSD([sQuery(id+"F7.wireOp",EDGE,"E67")])],"isStart":false})]});
            var Q2;
            Q2=makeQuery(id+"F8.boolean.opBoolean","INTERSECT",EDGE,{"disambiguationData":[OD(1.0)],"derivedFrom":[makeQuery(id+"F5.opExtrude","SWEPT_FACE",FACE,{"disambiguationData":[OSD([sQuery(id+"F4.wireOp",EDGE,"E30")])]}),makeQuery(id+"F8.opExtrude","SWEPT_FACE",FACE,{"disambiguationData":[OSD([sQuery(id+"F7.wireOp",EDGE,"E67")])]})]});
            var Q3;
            {var subQ0=sQuery(id+"F4.wireOp",EDGE,"E30");Q3=makeQuery(id+"F8.boolean.opBoolean","SPLIT",EDGE,{"disambiguationData":[TD([makeQuery(id+"F5.opExtrude","SWEPT_FACE",FACE,{"disambiguationData":[OSD([sQuery(id+"F4.wireOp",EDGE,"E35.filletArc")])]})])],"derivedFrom":makeQuery(id+"F5.opExtrude","CAP_EDGE",EDGE,{"disambiguationData":[OSD([subQ0])],"isStart":false})});}
            var Q4;
            {var subQ0=sQuery(id+"F0.wireOp",EDGE,"E25.7");var subQ1=sQuery(id+"F0.wireOp",EDGE,"E25.1");var subQ2=sQuery(id+"F0.wireOp",EDGE,"E25.6");var subQ3=sQuery(id+"F0.wireOp",EDGE,"E25.5");var subQ4=sQuery(id+"F0.wireOp",EDGE,"E25.4");var subQ5=sQuery(id+"F0.wireOp",EDGE,"E25.0");var subQ6=sQuery(id+"F0.wireOp",EDGE,"E25.2");var subQ7=sQuery(id+"F0.wireOp",EDGE,"E25.3");Q4=makeQuery(id+"F8.boolean.opBoolean","INTERSECT",EDGE,{"derivedFrom":[makeQuery(id+"F5.boolean.opBoolean","SPLIT",FACE,{"disambiguationData":[TD([makeQuery(id+"F2.opExtrude","SWEPT_FACE",FACE,{"disambiguationData":[OSD([subQ5])]})])],"derivedFrom":makeQuery(id+"F3.boolean.opBoolean","COPY",FACE,{"derivedFrom":makeQuery(id+"F3.opExtrude","CAP_FACE",FACE,{"disambiguationData":[OSD([subQ5,subQ1,subQ6,subQ7,subQ4,subQ3,subQ2,subQ0])],"isStart":false})})}),makeQuery(id+"F8.opExtrude","SWEPT_FACE",FACE,{"disambiguationData":[OSD([sQuery(id+"F7.wireOp",EDGE,"E67")])]})]});}
            var Q5;
            Q5=makeQuery(id+"F8.boolean.opBoolean","INTERSECT",EDGE,{"disambiguationData":[OD(0.0)],"derivedFrom":[makeQuery(id+"F5.opExtrude","SWEPT_FACE",FACE,{"disambiguationData":[OSD([sQuery(id+"F4.wireOp",EDGE,"E30")])]}),makeQuery(id+"F8.opExtrude","SWEPT_FACE",FACE,{"disambiguationData":[OSD([sQuery(id+"F7.wireOp",EDGE,"E67")])]})]});
            fillet(context, id + "F14", {"entities" : qUnion([Q0, Q1, Q2, Q3, Q4, Q5]), "radius" : 3 * mm, "tangentPropagation" : true, "allowEdgeOverflow" : false});
        }
        {
            var Q0;
            Q0=makeQuery(id+"F1.opExtrude","CAP_EDGE",EDGE,{"disambiguationData":[OSD([sQuery(id+"F0.wireOp",EDGE,"E1.bottom")])],"isStart":false});
            fillet(context, id + "F15", {"entities" : qUnion([Q0]), "radius" : 2 * mm, "tangentPropagation" : true, "allowEdgeOverflow" : false});
        }
        {
            var Q0;
            {var subQ0=sQuery(id+"F0.wireOp",EDGE,"E21.filletArc");var subQ1=sQuery(id+"F0.wireOp",EDGE,"E7");var subQ2=sQuery(id+"F0.wireOp",EDGE,"E6");var subQ3=sQuery(id+"F0.wireOp",EDGE,"E5");var subQ4=sQuery(id+"F0.wireOp",EDGE,"E4");var subQ5=sQuery(id+"F0.wireOp",EDGE,"E22.filletArc");var subQ6=sQuery(id+"F0.wireOp",EDGE,"E1.bottom");var subQ7=sQuery(id+"F0.wireOp",EDGE,"E1.right");var subQ8=sQuery(id+"F0.wireOp",EDGE,"E1.top");var subQ9=sQuery(id+"F0.wireOp",EDGE,"E1.left");var subQ10=sQuery(id+"F0.wireOp",EDGE,"E23.filletArc");var subQ11=sQuery(id+"F0.wireOp",EDGE,"E24.filletArc");Q0=makeQuery(id+"F2.boolean.opBoolean","SPLIT",FACE,{"disambiguationData":[TD([makeQuery(id+"F1.opExtrude","SWEPT_FACE",FACE,{"disambiguationData":[OSD([subQ6])]})])],"derivedFrom":makeQuery(id+"F1.opExtrude","CAP_FACE",FACE,{"disambiguationData":[OSD([subQ6,subQ8,subQ9,subQ7,subQ4,subQ3,subQ2,subQ1,subQ0,subQ5,subQ10,subQ11])],"isStart":true})});}
            var sketch = newSketch(context, id + "F16", { "sketchPlane" : qUnion([Q0])});
            skLineSegment(sketch, "E79", {"start": v(0, -90) * mm, "end": v(0, -120) * mm, "construction": true});
            skCircle(sketch, "E80", {"center": v(0, -120) * mm, "radius": 6 * mm});
            skArc(sketch, "E81", {"start": v(-15, -120) * mm, "mid": v(0, -135) * mm, "end": v(15, -120) * mm});
            skLineSegment(sketch, "E82", {"start": v(15, -120) * mm, "end": v(15, -108) * mm});
            skLineSegment(sketch, "E83", {"start": v(15, -108) * mm, "end": v(33, -90) * mm});
            skLineSegment(sketch, "E84", {"start": v(-15, -120) * mm, "end": v(-15, -108) * mm});
            skLineSegment(sketch, "E85", {"start": v(-15, -108) * mm, "end": v(-33, -90) * mm});
            skLineSegment(sketch, "E86", {"start": v(80, 0) * mm, "end": v(-80, 0) * mm, "construction": true});
            skCircle(sketch, "E87.MirrorC", {"center": v(0, 120) * mm, "radius": 6 * mm});
            skLineSegment(sketch, "E88.MirrorCS", {"start": v(-15, 120) * mm, "end": v(-15, 108) * mm});
            skLineSegment(sketch, "E89.MirrorCS", {"start": v(15, 120) * mm, "end": v(15, 108) * mm});
            skArc(sketch, "E90.MirrorCS", {"start": v(-15, 120) * mm, "mid": v(0, 135) * mm, "end": v(15, 120) * mm});
            skLineSegment(sketch, "E91.MirrorCS", {"start": v(15, 108) * mm, "end": v(33, 90) * mm});
            skLineSegment(sketch, "E92.MirrorCS", {"start": v(-15, 108) * mm, "end": v(-33, 90) * mm});
            skSolve(sketch);
        }
        {
            var Q0;
            Q0=makeQuery(id+"F16.imprint","IMPRINT",FACE,{"disambiguationData":[TD([[makeQuery(id+"F16.imprint","IMPRINT",EDGE,{"derivedFrom":sQuery(id+"F16.wireOp",EDGE,"E80")}),-1.0]])]});
            var Q1;
            Q1=makeQuery(id+"F16.imprint","IMPRINT",FACE,{"disambiguationData":[TD([[makeQuery(id+"F16.imprint","IMPRINT",EDGE,{"derivedFrom":makeQuery(id+"F1.opExtrude","CAP_EDGE",EDGE,{"disambiguationData":[OSD([sQuery(id+"F0.wireOp",EDGE,"E1.left")])],"isStart":true})}),-1.0]])]});
            var Q2;
            Q2=makeQuery(id+"F16.imprint","IMPRINT",FACE,{"disambiguationData":[TD([[makeQuery(id+"F16.imprint","IMPRINT",EDGE,{"derivedFrom":sQuery(id+"F16.wireOp",EDGE,"E88.MirrorCS")}),1.0]])]});
            var Q3;
            Q3=makeQuery(id+"F2.opExtrude","CAP_FACE",FACE,{"disambiguationData":[OSD([sQuery(id+"F0.wireOp",EDGE,"E12"),sQuery(id+"F0.wireOp",EDGE,"E13"),sQuery(id+"F0.wireOp",EDGE,"E14"),sQuery(id+"F0.wireOp",EDGE,"E15"),sQuery(id+"F0.wireOp",EDGE,"E17.filletArc"),sQuery(id+"F0.wireOp",EDGE,"E18.filletArc"),sQuery(id+"F0.wireOp",EDGE,"E19.filletArc"),sQuery(id+"F0.wireOp",EDGE,"E20.filletArc"),sQuery(id+"F0.wireOp",EDGE,"E25.0"),sQuery(id+"F0.wireOp",EDGE,"E25.1"),sQuery(id+"F0.wireOp",EDGE,"E25.2"),sQuery(id+"F0.wireOp",EDGE,"E25.3"),sQuery(id+"F0.wireOp",EDGE,"E25.4"),sQuery(id+"F0.wireOp",EDGE,"E25.5"),sQuery(id+"F0.wireOp",EDGE,"E25.6"),sQuery(id+"F0.wireOp",EDGE,"E25.7")])],"isStart":false});
            extrude(context, id + "F17", {"entities" : qUnion([Q0, Q1, Q2]), "endBound" : BoundingType.UP_TO_SURFACE, "depth" : 25 * mm, "endBoundEntityFace" : qUnion([Q3]), "offsetDistance" : 25 * mm});
        }
    });
